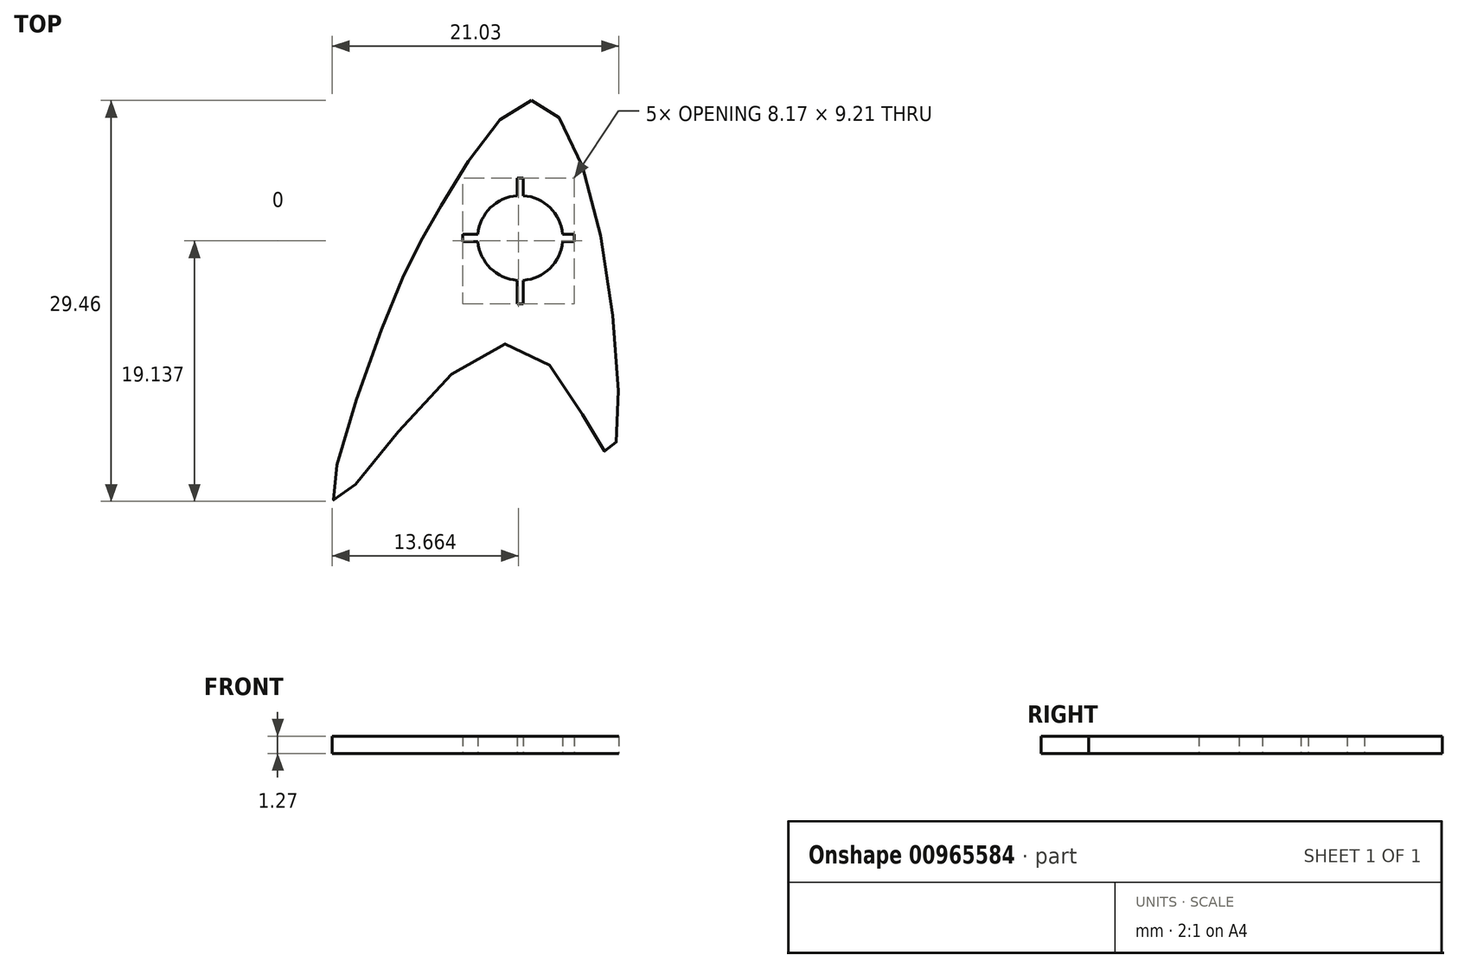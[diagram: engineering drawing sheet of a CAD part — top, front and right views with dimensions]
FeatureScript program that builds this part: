
annotation { "Feature Type Name" : "Feature", "Feature Type Description" : "" }
export const myFeature = defineFeature(function(context is Context, id is Id, definition is map)
    precondition{}
    {
        {
            var Q0;
            Q0=qCreatedBy(makeId("Top.planeOp"),FACE);
            var sketch = newSketch(context, id + "F0", { "sketchPlane" : qUnion([Q0])});
            skFitSpline(sketch, "E0", {"points": [v(-50.32, 50.29) * mm, v(-56.85, 42.73) * mm, v(-60.9, 34.58) * mm, v(-64.63, 20.83) * mm, v(-51.84, 32.41) * mm, v(-44.76, 24.35) * mm, v(-44.82, 37.97) * mm, v(-50.32, 50.29) * mm]});
            skCircle(sketch, "E1", {"center": v(-51.14, 40.19) * mm, "radius": 3.12 * mm});
            skLineSegment(sketch, "E2.bottom", {"start": v(-51.36, 44.57) * mm, "end": v(-50.92, 44.57) * mm});
            skLineSegment(sketch, "E2.top", {"start": v(-51.36, 35.36) * mm, "end": v(-50.92, 35.36) * mm});
            skLineSegment(sketch, "E2.left", {"start": v(-51.36, 44.57) * mm, "end": v(-51.36, 35.36) * mm});
            skLineSegment(sketch, "E2.right", {"start": v(-50.92, 44.57) * mm, "end": v(-50.92, 35.36) * mm});
            skLineSegment(sketch, "E3.bottom", {"start": v(-55.36, 40.46) * mm, "end": v(-47.19, 40.46) * mm});
            skLineSegment(sketch, "E3.top", {"start": v(-55.36, 39.91) * mm, "end": v(-47.19, 39.91) * mm});
            skLineSegment(sketch, "E3.left", {"start": v(-55.36, 40.46) * mm, "end": v(-55.36, 39.91) * mm});
            skLineSegment(sketch, "E3.right", {"start": v(-47.19, 40.46) * mm, "end": v(-47.19, 39.91) * mm});
            skSolve(sketch);
        }
        {
            var Q0;
            Q0 = qSketchRegion(id + "F0", true);
            extrude(context, id + "F1", {"entities" : qUnion([Q0]), "depth" : 1.27 * mm, "offsetDistance" : 25.4 * mm});
        }
    });
